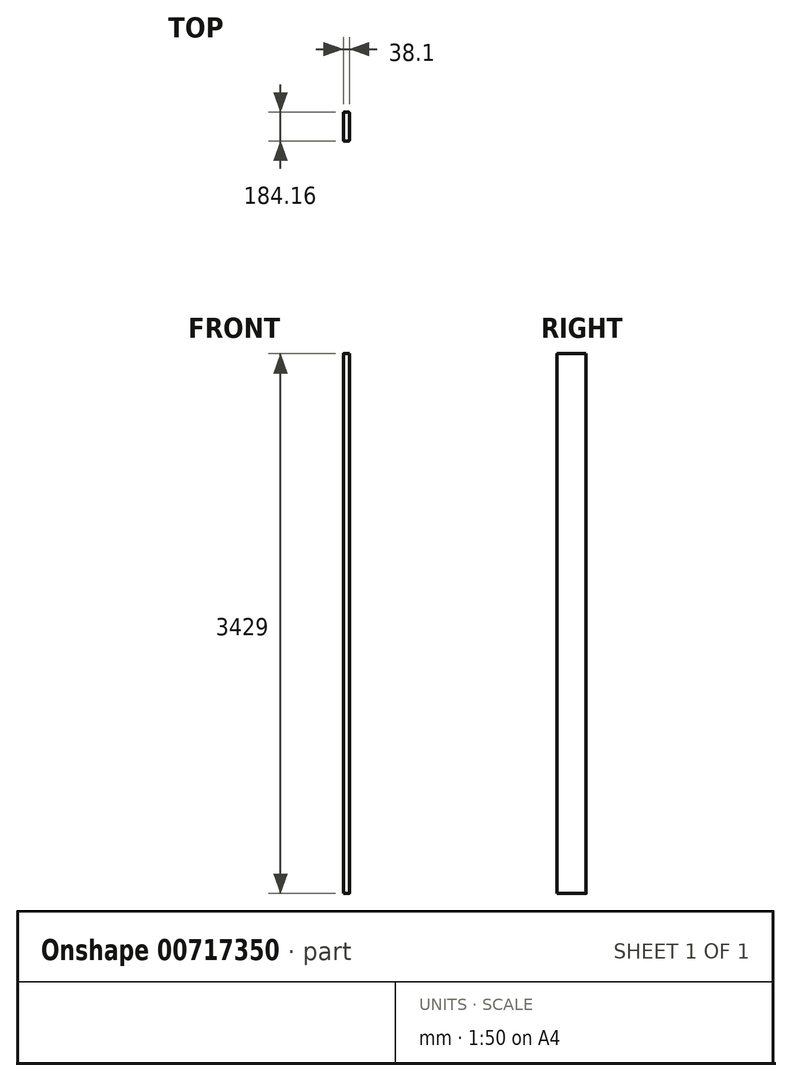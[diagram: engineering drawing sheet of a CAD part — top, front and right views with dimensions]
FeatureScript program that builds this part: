
annotation { "Feature Type Name" : "Feature", "Feature Type Description" : "" }
export const myFeature = defineFeature(function(context is Context, id is Id, definition is map)
    precondition{}
    {
        {
            var Q0;
            Q0=qCreatedBy(makeId("Top.planeOp"),FACE);
            var sketch = newSketch(context, id + "F0", { "sketchPlane" : qUnion([Q0])});
            skLineSegment(sketch, "E0.bottom", {"start": v(-12.7, 92.08) * mm, "end": v(12.7, 92.08) * mm});
            skLineSegment(sketch, "E0.top", {"start": v(-12.7, -92.08) * mm, "end": v(12.7, -92.08) * mm});
            skLineSegment(sketch, "E0.left", {"start": v(-19.05, 85.73) * mm, "end": v(-19.05, -85.73) * mm});
            skLineSegment(sketch, "E0.right", {"start": v(19.05, 85.73) * mm, "end": v(19.05, -85.73) * mm});
            skLineSegment(sketch, "E1", {"start": v(-19.05, -92.08) * mm, "end": v(19.05, 92.08) * mm, "construction": true});
            skPoint(sketch, "E2.visualSharp", {"position": v(19.05, 92.08) * mm});
            skArc(sketch, "E2.filletArc", {"start": v(19.05, 85.73) * mm, "mid": v(17.2, 90.22) * mm, "end": v(12.7, 92.08) * mm});
            skPoint(sketch, "E3.visualSharp", {"position": v(-19.05, 92.08) * mm});
            skArc(sketch, "E3.filletArc", {"start": v(-12.7, 92.08) * mm, "mid": v(-17.2, 90.22) * mm, "end": v(-19.05, 85.73) * mm});
            skPoint(sketch, "E4.visualSharp", {"position": v(-19.05, -92.08) * mm});
            skArc(sketch, "E4.filletArc", {"start": v(-19.05, -85.73) * mm, "mid": v(-17.2, -90.22) * mm, "end": v(-12.7, -92.08) * mm});
            skPoint(sketch, "E5.visualSharp", {"position": v(19.05, -92.08) * mm});
            skArc(sketch, "E5.filletArc", {"start": v(12.7, -92.08) * mm, "mid": v(17.2, -90.22) * mm, "end": v(19.05, -85.73) * mm});
            skSolve(sketch);
        }
        {
            var Q0;
            Q0=makeQuery(id+"F0.imprint","IMPRINT",FACE,{"disambiguationData":[TD([[makeQuery(id+"F0.imprint","IMPRINT",EDGE,{"derivedFrom":sQuery(id+"F0.wireOp",EDGE,"E0.bottom")}),-1.0]])]});
            extrude(context, id + "F1", {"entities" : qUnion([Q0]), "depth" : 3429 * mm, "offsetDistance" : 25.4 * mm});
        }
    });
